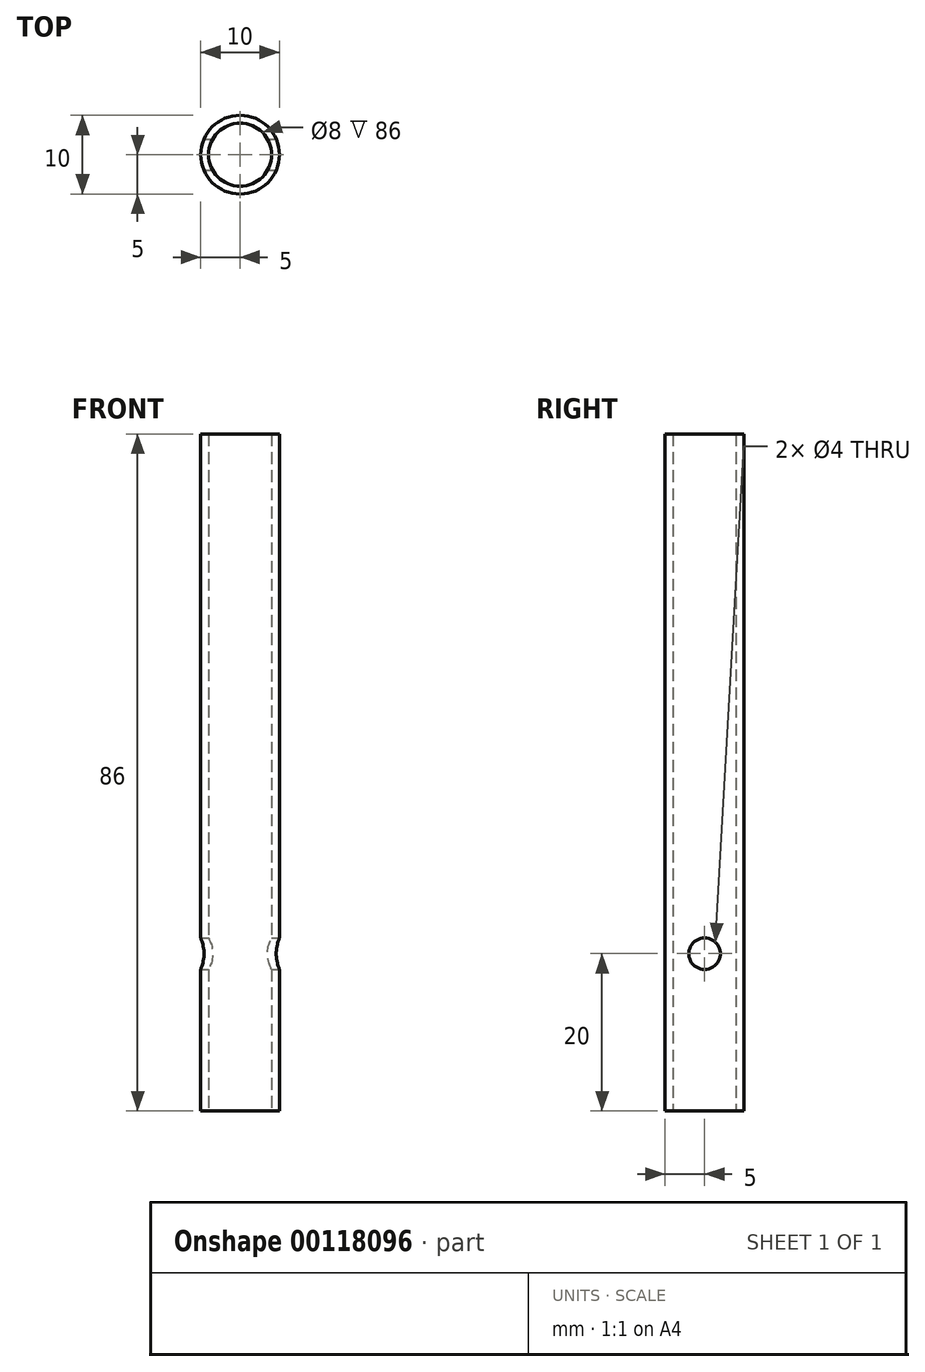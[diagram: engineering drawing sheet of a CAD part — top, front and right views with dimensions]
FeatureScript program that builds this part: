
annotation { "Feature Type Name" : "Feature", "Feature Type Description" : "" }
export const myFeature = defineFeature(function(context is Context, id is Id, definition is map)
    precondition{}
    {
        {
            var Q0;
            Q0=qCreatedBy(makeId("Top.planeOp"),FACE);
            var sketch = newSketch(context, id + "F0", { "sketchPlane" : qUnion([Q0])});
            skCircle(sketch, "E0", {"center": v(0, 0) * mm, "radius": 4 * mm});
            skCircle(sketch, "E1", {"center": v(0, 0) * mm, "radius": 5 * mm});
            skSolve(sketch);
        }
        {
            var Q0;
            Q0=makeQuery(id+"F0.imprint","IMPRINT",FACE,{"disambiguationData":[TD([[makeQuery(id+"F0.imprint","IMPRINT",EDGE,{"derivedFrom":sQuery(id+"F0.wireOp",EDGE,"E0")}),-1.0]])]});
            extrude(context, id + "F1", {"entities" : qUnion([Q0]), "depth" : 86 * mm});
        }
        {
            var Q0;
            Q0=qCreatedBy(makeId("Right.planeOp"),FACE);
            cPlane(context, id + "F2", {"entities" : qUnion([Q0]), "cplaneType" : CPlaneType.OFFSET, "offset" : 5 * mm, "width" : 150 * mm, "height" : 150 * mm});
        }
        {
            var Q0;
            Q0=qCreatedBy(id+"F2.planeOp",FACE);
            var sketch = newSketch(context, id + "F3", { "sketchPlane" : qUnion([Q0])});
            skLineSegment(sketch, "E2", {"start": v(0, 0) * mm, "end": v(0, 20) * mm, "construction": true});
            skCircle(sketch, "E3", {"center": v(0, 20) * mm, "radius": 2 * mm});
            skSolve(sketch);
        }
        {
            var Q0;
            Q0=makeQuery(id+"F3.imprint","IMPRINT",FACE,{"disambiguationData":[TD([[makeQuery(id+"F3.imprint","IMPRINT",EDGE,{"derivedFrom":sQuery(id+"F3.wireOp",EDGE,"E3")}),1.0]])]});
            extrude(context, id + "F4", {"entities" : qUnion([Q0]), "operationType" : NewBodyOperationType.REMOVE, "oppositeDirection" : true, "depth" : 10 * mm});
        }
    });
